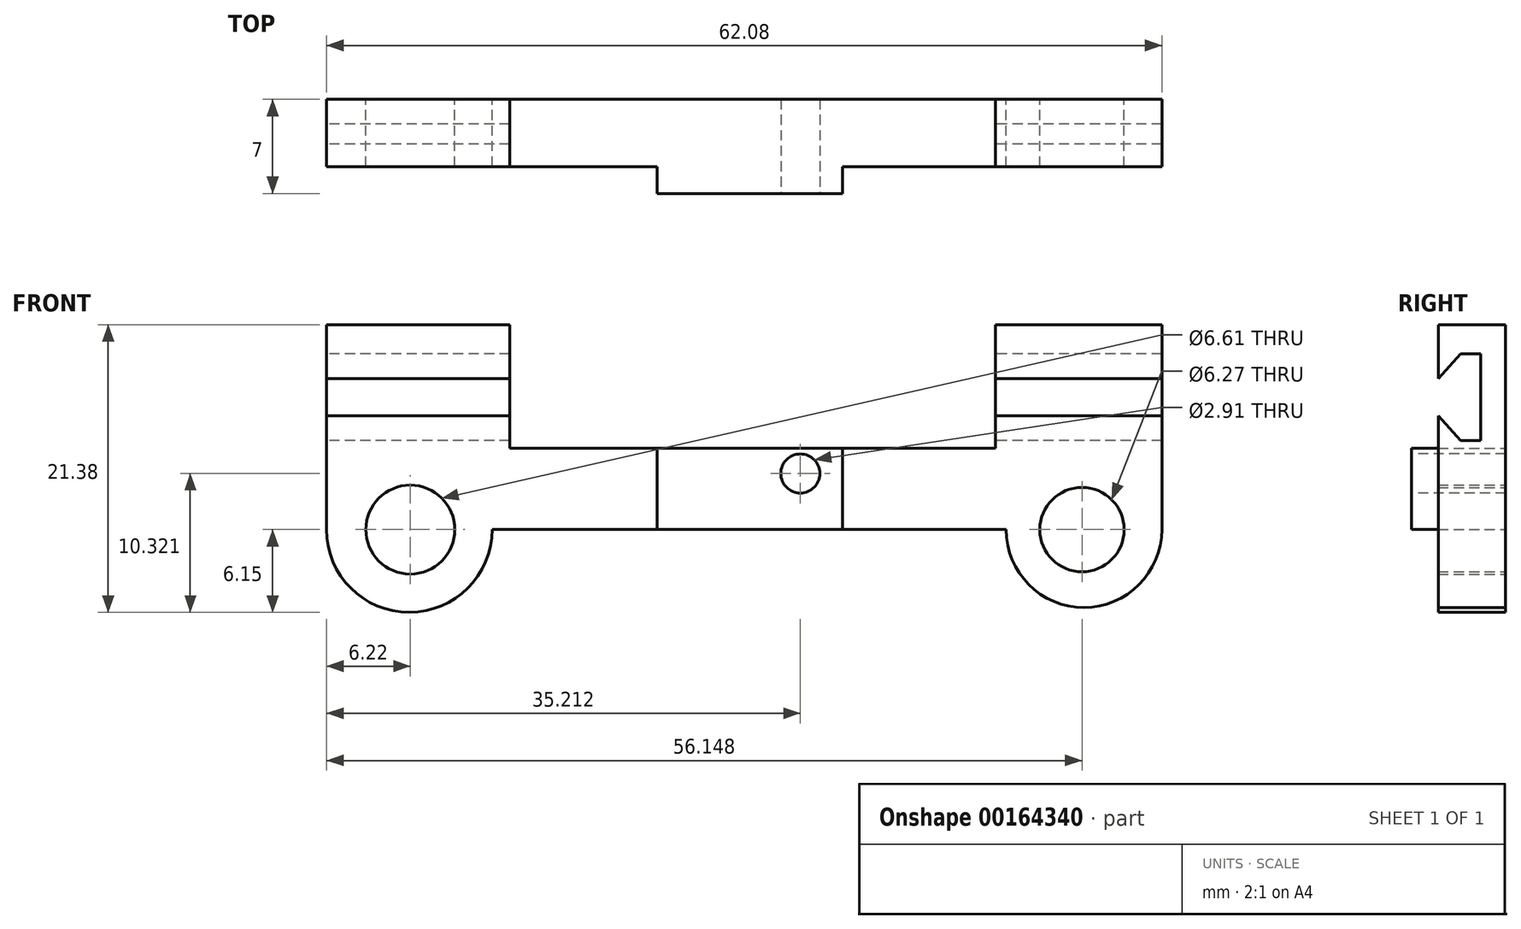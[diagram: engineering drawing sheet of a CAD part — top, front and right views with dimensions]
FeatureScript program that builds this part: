
annotation { "Feature Type Name" : "Feature", "Feature Type Description" : "" }
export const myFeature = defineFeature(function(context is Context, id is Id, definition is map)
    precondition{}
    {
        {
            var Q0;
            Q0=qCreatedBy(makeId("Front.planeOp"),FACE);
            var sketch = newSketch(context, id + "F0", { "sketchPlane" : qUnion([Q0])});
            skCircle(sketch, "E0", {"center": v(-25.22, 0) * mm, "radius": 3.3 * mm});
            skCircle(sketch, "E1", {"center": v(24.7, 0) * mm, "radius": 3.14 * mm});
            skArc(sketch, "E2", {"start": v(-31.44, 0) * mm, "mid": v(-25.3, -6.15) * mm, "end": v(-19.14, 0) * mm});
            skArc(sketch, "E3", {"start": v(19.06, 0) * mm, "mid": v(24.85, -5.79) * mm, "end": v(30.64, 0) * mm});
            skLineSegment(sketch, "E4", {"start": v(-31.44, 0) * mm, "end": v(-31.44, 15.23) * mm});
            skLineSegment(sketch, "E5", {"start": v(-31.44, 15.23) * mm, "end": v(-17.83, 15.23) * mm});
            skLineSegment(sketch, "E6", {"start": v(-17.83, 15.23) * mm, "end": v(-17.83, 6.05) * mm});
            skLineSegment(sketch, "E7", {"start": v(-17.83, 6.05) * mm, "end": v(18.27, 6.05) * mm});
            skLineSegment(sketch, "E8", {"start": v(18.27, 6.05) * mm, "end": v(18.27, 15.23) * mm});
            skLineSegment(sketch, "E9", {"start": v(18.27, 15.23) * mm, "end": v(30.64, 15.23) * mm});
            skLineSegment(sketch, "E10", {"start": v(30.64, 15.23) * mm, "end": v(30.64, 0) * mm});
            skLineSegment(sketch, "E11", {"start": v(19.06, 0) * mm, "end": v(-19.14, 0) * mm});
            skSolve(sketch);
        }
        {
            var Q0;
            Q0 = qSketchRegion(id + "F0", true);
            extrude(context, id + "F1", {"entities" : qUnion([Q0]), "depth" : 5 * mm});
        }
        {
            var Q0;
            Q0=makeQuery(id+"F1.opExtrude","SWEPT_FACE",FACE,{"disambiguationData":[OSD([sQuery(id+"F0.wireOp",EDGE,"E4")])]});
            var sketch = newSketch(context, id + "F2", { "sketchPlane" : qUnion([Q0])});
            skLineSegment(sketch, "E12", {"start": v(1.84, 13.06) * mm, "end": v(1.84, 6.63) * mm});
            skLineSegment(sketch, "E13", {"start": v(1.84, 13.06) * mm, "end": v(3.34, 13.06) * mm});
            skLineSegment(sketch, "E14", {"start": v(3.34, 13.06) * mm, "end": v(5, 11.23) * mm});
            skLineSegment(sketch, "E15", {"start": v(1.84, 6.63) * mm, "end": v(3.34, 6.63) * mm});
            skLineSegment(sketch, "E16", {"start": v(3.34, 6.63) * mm, "end": v(5, 8.46) * mm});
            skSolve(sketch);
        }
        {
            var Q0;
            Q0=makeQuery(id+"F2.imprint","IMPRINT",FACE,{"disambiguationData":[TD([[makeQuery(id+"F2.imprint","IMPRINT",EDGE,{"derivedFrom":sQuery(id+"F2.wireOp",EDGE,"E12")}),1.0]])]});
            extrude(context, id + "F3", {"entities" : qUnion([Q0]), "operationType" : NewBodyOperationType.REMOVE, "endBound" : BoundingType.THROUGH_ALL, "oppositeDirection" : true, "depth" : 25 * mm});
        }
        {
            var Q0;
            {var subQ0=sQuery(id+"F0.wireOp",EDGE,"E11");var subQ1=sQuery(id+"F0.wireOp",EDGE,"E10");var subQ2=sQuery(id+"F0.wireOp",EDGE,"E8");var subQ3=sQuery(id+"F0.wireOp",EDGE,"E7");var subQ4=sQuery(id+"F0.wireOp",EDGE,"E6");var subQ5=sQuery(id+"F0.wireOp",EDGE,"E4");var subQ6=sQuery(id+"F0.wireOp",EDGE,"E0");var subQ7=sQuery(id+"F0.wireOp",EDGE,"E3");var subQ8=sQuery(id+"F0.wireOp",EDGE,"E1");var subQ9=sQuery(id+"F0.wireOp",EDGE,"E2");Q0=makeQuery(id+"F3.boolean.opBoolean","SPLIT",FACE,{"disambiguationData":[TD([makeQuery(id+"F1.opExtrude","SWEPT_FACE",FACE,{"disambiguationData":[OSD([subQ6])]})])],"derivedFrom":makeQuery(id+"F1.opExtrude","CAP_FACE",FACE,{"disambiguationData":[OSD([subQ6,subQ8,subQ9,subQ7,subQ5,sQuery(id+"F0.wireOp",EDGE,"E5"),subQ4,subQ3,subQ2,sQuery(id+"F0.wireOp",EDGE,"E9"),subQ1,subQ0])],"isStart":false})});}
            var sketch = newSketch(context, id + "F4", { "sketchPlane" : qUnion([Q0])});
            skLineSegment(sketch, "E17.bottom", {"start": v(-6.87, 6.05) * mm, "end": v(6.9, 6.05) * mm});
            skLineSegment(sketch, "E17.top", {"start": v(-6.87, 0) * mm, "end": v(6.9, 0) * mm});
            skLineSegment(sketch, "E17.left", {"start": v(-6.87, 6.05) * mm, "end": v(-6.87, 0) * mm});
            skLineSegment(sketch, "E17.right", {"start": v(6.9, 6.05) * mm, "end": v(6.9, 0) * mm});
            skSolve(sketch);
        }
        {
            var Q0;
            Q0 = qSketchRegion(id + "F4", true);
            extrude(context, id + "F5", {"entities" : qUnion([Q0]), "operationType" : NewBodyOperationType.ADD, "depth" : 2 * mm});
        }
        {
            var Q0;
            Q0=makeQuery(id+"F5.opExtrude","CAP_FACE",FACE,{"disambiguationData":[OSD([sQuery(id+"F4.wireOp",EDGE,"E17.bottom"),sQuery(id+"F4.wireOp",EDGE,"E17.top"),sQuery(id+"F4.wireOp",EDGE,"E17.left"),sQuery(id+"F4.wireOp",EDGE,"E17.right")])],"isStart":false});
            var sketch = newSketch(context, id + "F6", { "sketchPlane" : qUnion([Q0])});
            skCircle(sketch, "E18", {"center": v(3.77, 4.17) * mm, "radius": 1.45 * mm});
            skPoint(sketch, "E18.centerSnap0", {"position": v(6.9, 3.03) * mm});
            skPoint(sketch, "E18.centerSnap1", {"position": v(0.02, 6.05) * mm});
            skSolve(sketch);
        }
        {
            var Q0;
            Q0 = qSketchRegion(id + "F6", true);
            extrude(context, id + "F7", {"entities" : qUnion([Q0]), "operationType" : NewBodyOperationType.REMOVE, "oppositeDirection" : true, "depth" : 25 * mm});
        }
    });
